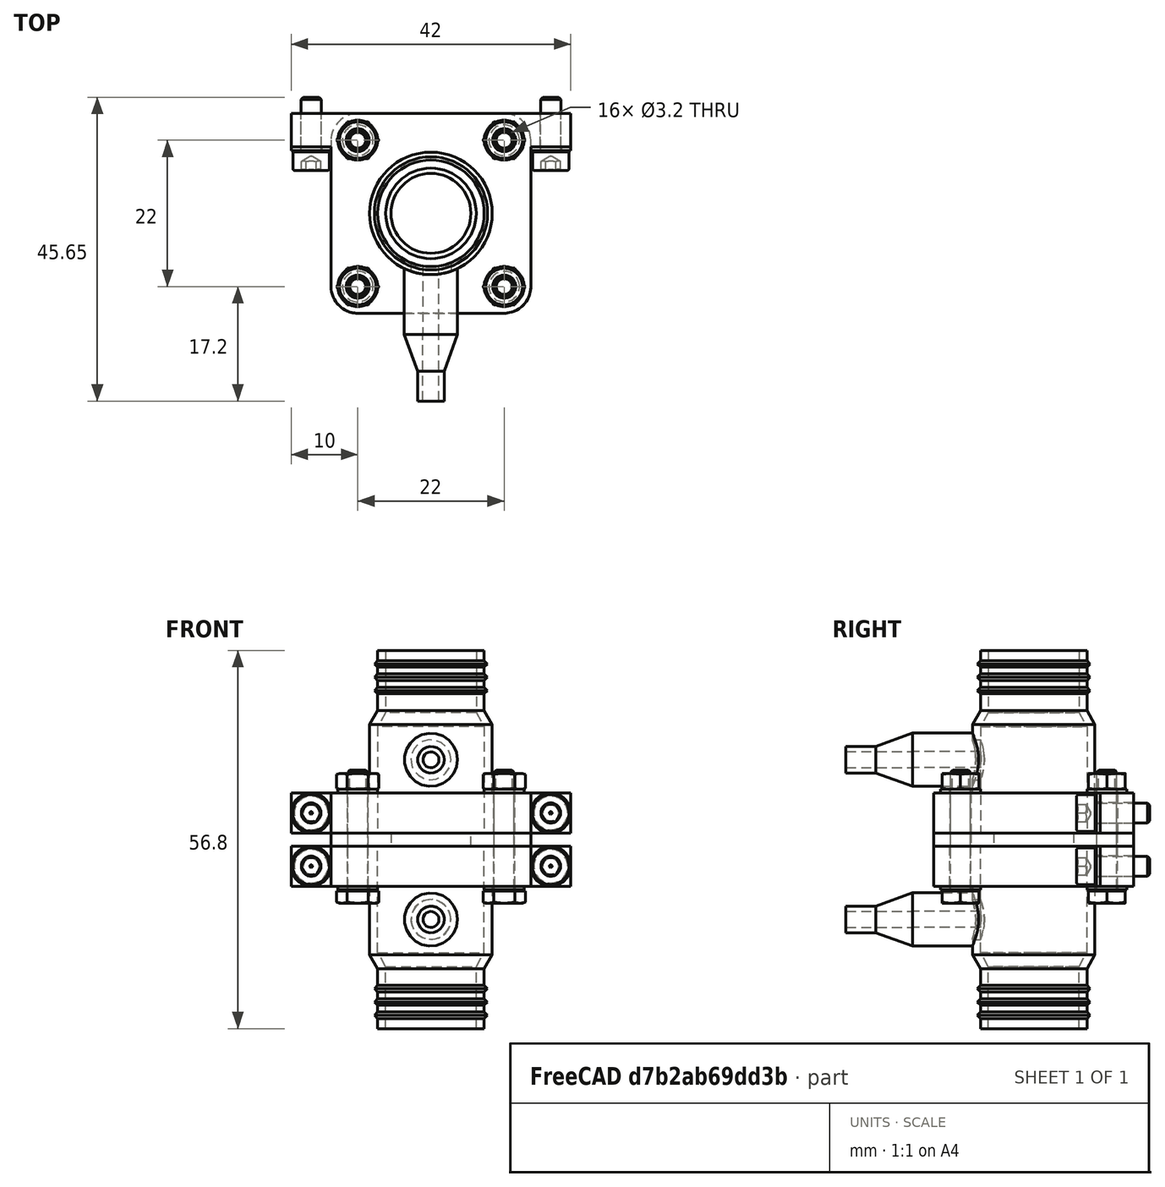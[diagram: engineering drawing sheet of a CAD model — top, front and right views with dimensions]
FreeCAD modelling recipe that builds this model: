
FCSTD DOCUMENT  (FreeCAD 0.19R20655 (Git))
Label: flowmeter_assembly
License: All rights reserved
LicenseURL: http://en.wikipedia.org/wiki/All_rights_reserved
objects: Part::FeaturePython×29, App::FeaturePython×18
note: 29 computed .brp shape members not serialized (recipe doc carries the construction recipe); baked Part::Feature solids carry a one-line shape summary decoded from their .brp

FEATURE [Part::FeaturePython] b_housing_001_  label="housing_001"  # a2plus imported part (geometry in sourceFile) (typed FeaturePython)
  a2p_Version = V0.1
  fixedPosition = true
  objectType = a2pPart
  sourceFile = .\housing.FCStd
  subassemblyImport = false
  timeLastImport = 1.58808e+09
  updateColors = true
FEATURE [Part::FeaturePython] b_gasket_001_  label="orifice_001"  # a2plus imported part (geometry in sourceFile) (typed FeaturePython)
  Placement = pos=(-3.70546e-08,-3.70546e-08,-2) rot=(0,0,1;0rad)
  a2p_Version = V0.1
  fixedPosition = false
  objectType = a2pPart
  sourceFile = .\gasket.FCStd
  subassemblyImport = false
  timeLastImport = 1.58802e+09
  updateColors = true
FEATURE [App::FeaturePython] axisCoincident_001  label="axisCoincident_001__housing_001"  # a2plus constraint (typed FeaturePython)
  Object1 = b_gasket_001_
  Object2 = b_housing_001_
  ParentTreeObject = -> b_gasket_001_
  SubElement1 = Face11
  SubElement2 = Face13
  Suppressed = false
  Type = axial
  directionConstraint = 0
  lockRotation = false
  suppressed = false
FEATURE [App::FeaturePython] axisCoincident_001_mirror  label="axisCoincident_001__gasket_001"  # a2plus constraint (typed FeaturePython)
  Object1 = b_gasket_001_
  Object2 = b_housing_001_
  ParentTreeObject = -> b_housing_001_
  SubElement1 = Face11
  SubElement2 = Face13
  Suppressed = false
  Type = axial
  directionConstraint = 0
  lockRotation = false
  suppressed = false
FEATURE [App::FeaturePython] axisCoincident_002  label="axisCoincident_002__housing_001"  # a2plus constraint (typed FeaturePython)
  Object1 = b_gasket_001_
  Object2 = b_housing_001_
  ParentTreeObject = -> b_gasket_001_
  SubElement1 = Face13
  SubElement2 = Face17
  Suppressed = false
  Type = axial
  directionConstraint = 0
  lockRotation = false
  suppressed = false
FEATURE [App::FeaturePython] axisCoincident_002_mirror  label="axisCoincident_002__gasket_001"  # a2plus constraint (typed FeaturePython)
  Object1 = b_gasket_001_
  Object2 = b_housing_001_
  ParentTreeObject = -> b_housing_001_
  SubElement1 = Face13
  SubElement2 = Face17
  Suppressed = false
  Type = axial
  directionConstraint = 0
  lockRotation = false
  suppressed = false
FEATURE [App::FeaturePython] planeCoincident_001  label="planeCoincident_001__housing_001"  # a2plus constraint (typed FeaturePython)
  Object1 = b_gasket_001_
  Object2 = b_housing_001_
  ParentTreeObject = -> b_gasket_001_
  SubElement1 = Face5
  SubElement2 = Face2
  Suppressed = false
  Type = plane
  directionConstraint = 1
  offset = 0
  suppressed = false
FEATURE [App::FeaturePython] planeCoincident_001_mirror  label="planeCoincident_001__gasket_001"  # a2plus constraint (typed FeaturePython)
  Object1 = b_gasket_001_
  Object2 = b_housing_001_
  ParentTreeObject = -> b_housing_001_
  SubElement1 = Face5
  SubElement2 = Face2
  Suppressed = false
  Type = plane
  directionConstraint = 1
  offset = 0
  suppressed = false
FEATURE [Part::FeaturePython] b_housing_001_001  label="housing_002"  # a2plus imported part (geometry in sourceFile) (typed FeaturePython)
  Placement = pos=(1.75624e-07,1e-15,-2) rot=(0,1,0;3.14159rad)
  a2p_Version = V0.1
  fixedPosition = false
  objectType = a2pPart
  sourceFile = .\housing.FCStd
  subassemblyImport = false
  timeLastImport = 1.58808e+09
  updateColors = true
FEATURE [App::FeaturePython] axisCoincident_003  label="axisCoincident_003__housing_001"  # a2plus constraint (typed FeaturePython)
  Object1 = b_housing_001_001
  Object2 = b_housing_001_
  ParentTreeObject = -> b_housing_001_001
  SubElement1 = Face18
  SubElement2 = Face13
  Suppressed = false
  Type = axial
  directionConstraint = 0
  lockRotation = false
  suppressed = false
FEATURE [App::FeaturePython] axisCoincident_003_mirror  label="axisCoincident_003__housing_002"  # a2plus constraint (typed FeaturePython)
  Object1 = b_housing_001_001
  Object2 = b_housing_001_
  ParentTreeObject = -> b_housing_001_
  SubElement1 = Face18
  SubElement2 = Face13
  Suppressed = false
  Type = axial
  directionConstraint = 0
  lockRotation = false
  suppressed = false
FEATURE [App::FeaturePython] planeCoincident_002  label="planeCoincident_002__gasket_001"  # a2plus constraint (typed FeaturePython)
  Object1 = b_housing_001_001
  Object2 = b_gasket_001_
  ParentTreeObject = -> b_housing_001_001
  SubElement1 = Face2
  SubElement2 = Face2
  Suppressed = false
  Type = plane
  directionConstraint = 0
  offset = 0
  suppressed = false
FEATURE [App::FeaturePython] planeCoincident_002_mirror  label="planeCoincident_002__housing_002"  # a2plus constraint (typed FeaturePython)
  Object1 = b_housing_001_001
  Object2 = b_gasket_001_
  ParentTreeObject = -> b_gasket_001_
  SubElement1 = Face2
  SubElement2 = Face2
  Suppressed = false
  Type = plane
  directionConstraint = 0
  offset = 0
  suppressed = false
FEATURE [App::FeaturePython] planeCoincident_003  label="planeCoincident_003__housing_002"  # a2plus constraint (typed FeaturePython)
  Object1 = b_housing_001_
  Object2 = b_housing_001_001
  ParentTreeObject = -> b_housing_001_
  SubElement1 = Face1
  SubElement2 = Face1
  Suppressed = false
  Type = plane
  directionConstraint = 0
  offset = 0
  suppressed = false
FEATURE [App::FeaturePython] planeCoincident_003_mirror  label="planeCoincident_003__housing_001"  # a2plus constraint (typed FeaturePython)
  Object1 = b_housing_001_
  Object2 = b_housing_001_001
  ParentTreeObject = -> b_housing_001_001
  SubElement1 = Face1
  SubElement2 = Face1
  Suppressed = false
  Type = plane
  directionConstraint = 0
  offset = 0
  suppressed = false
FEATURE [Part::FeaturePython] b_pressure_connector_001_  label="pressure_connector_001"  # a2plus imported part (geometry in sourceFile) (typed FeaturePython)
  Placement = pos=(2.53008e-09,-8.2,-13) rot=(1,0,0;1.5708rad)
  a2p_Version = V0.1
  fixedPosition = false
  objectType = a2pPart
  sourceFile = .\pressure_connector.FCStd
  subassemblyImport = false
  timeLastImport = 1.58808e+09
  updateColors = true
FEATURE [App::FeaturePython] axisCoincident_004  label="axisCoincident_004__housing_002"  # a2plus constraint (typed FeaturePython)
  Object1 = b_pressure_connector_001_
  Object2 = b_housing_001_001
  ParentTreeObject = -> b_pressure_connector_001_
  SubElement1 = Face3
  SubElement2 = Face22
  Suppressed = false
  Type = axial
  directionConstraint = 0
  lockRotation = false
  suppressed = false
FEATURE [App::FeaturePython] axisCoincident_004_mirror  label="axisCoincident_004__pressure_connector_001"  # a2plus constraint (typed FeaturePython)
  Object1 = b_pressure_connector_001_
  Object2 = b_housing_001_001
  ParentTreeObject = -> b_housing_001_001
  SubElement1 = Face3
  SubElement2 = Face22
  Suppressed = false
  Type = axial
  directionConstraint = 0
  lockRotation = false
  suppressed = false
FEATURE [App::FeaturePython] axisCoincident_005  label="axisCoincident_005__pressure_connector_001"  # a2plus constraint (typed FeaturePython)
  Object1 = b_housing_001_001
  Object2 = b_pressure_connector_001_
  ParentTreeObject = -> b_housing_001_001
  SubElement1 = Face18
  SubElement2 = Face5
  Suppressed = false
  Type = axial
  directionConstraint = 1
  lockRotation = false
  suppressed = false
FEATURE [App::FeaturePython] axisCoincident_005_mirror  label="axisCoincident_005__housing_002"  # a2plus constraint (typed FeaturePython)
  Object1 = b_housing_001_001
  Object2 = b_pressure_connector_001_
  ParentTreeObject = -> b_pressure_connector_001_
  SubElement1 = Face18
  SubElement2 = Face5
  Suppressed = false
  Type = axial
  directionConstraint = 1
  lockRotation = false
  suppressed = false
FEATURE [Part::FeaturePython] b_pressure_connector_001_001  label="pressure_connector_002"  # a2plus imported part (geometry in sourceFile) (typed FeaturePython)
  Placement = pos=(-9e-15,-8.20001,11) rot=(1,0,0;1.5708rad)
  a2p_Version = V0.1
  fixedPosition = false
  objectType = a2pPart
  sourceFile = .\pressure_connector.FCStd
  subassemblyImport = false
  timeLastImport = 1.58808e+09
  updateColors = true
FEATURE [App::FeaturePython] axisCoincident_006  label="axisCoincident_006__housing_001"  # a2plus constraint (typed FeaturePython)
  Object1 = b_pressure_connector_001_001
  Object2 = b_housing_001_
  ParentTreeObject = -> b_pressure_connector_001_001
  SubElement1 = Face3
  SubElement2 = Face22
  Suppressed = false
  Type = axial
  directionConstraint = 0
  lockRotation = false
  suppressed = false
FEATURE [App::FeaturePython] axisCoincident_006_mirror  label="axisCoincident_006__pressure_connector_002"  # a2plus constraint (typed FeaturePython)
  Object1 = b_pressure_connector_001_001
  Object2 = b_housing_001_
  ParentTreeObject = -> b_housing_001_
  SubElement1 = Face3
  SubElement2 = Face22
  Suppressed = false
  Type = axial
  directionConstraint = 0
  lockRotation = false
  suppressed = false
FEATURE [Part::FeaturePython] Washer  label="M3-Washer"  # Fasteners workbench fastener (typed FeaturePython)
  Placement = pos=(18,10,-5) rot=(1,0,0;1.5708rad)
  baseObject = -> b_housing_001_001 [Edge37]
  diameter = 4
  invert = false
  matchOuter = true
  offset = 0
  type = 2
FEATURE [Part::FeaturePython] Washer001  label="M3-Washer001"  # Fasteners workbench fastener (typed FeaturePython)
  Placement = pos=(-18,10,-5) rot=(1,0,0;1.5708rad)
  baseObject = -> b_housing_001_001 [Edge44]
  diameter = 4
  invert = false
  matchOuter = true
  offset = 0
  type = 2
FEATURE [Part::FeaturePython] Washer002  label="M3-Washer002"  # Fasteners workbench fastener (typed FeaturePython)
  Placement = pos=(18,10,3) rot=(1,0,0;1.5708rad)
  baseObject = -> b_housing_001_ [Edge44]
  diameter = 4
  invert = false
  matchOuter = true
  offset = 0
  type = 2
FEATURE [Part::FeaturePython] Washer003  label="M3-Washer003"  # Fasteners workbench fastener (typed FeaturePython)
  Placement = pos=(-18,10,3) rot=(1,0,0;1.5708rad)
  baseObject = -> b_housing_001_ [Edge37]
  diameter = 4
  invert = false
  matchOuter = true
  offset = 0
  type = 2
FEATURE [Part::FeaturePython] Washer004  label="M3-Washer004"  # Fasteners workbench fastener (typed FeaturePython)
  Placement = pos=(11,11,-8) rot=(0,-1,0;3.14159rad)
  baseObject = -> b_housing_001_001 [Edge31]
  diameter = 4
  invert = false
  matchOuter = true
  offset = 0
  type = 2
FEATURE [Part::FeaturePython] Washer005  label="M3-Washer005"  # Fasteners workbench fastener (typed FeaturePython)
  Placement = pos=(11,-11,-8) rot=(0,-1,0;3.14159rad)
  baseObject = -> b_housing_001_001 [Edge34]
  diameter = 4
  invert = false
  matchOuter = true
  offset = 0
  type = 2
FEATURE [Part::FeaturePython] Washer006  label="M3-Washer006"  # Fasteners workbench fastener (typed FeaturePython)
  Placement = pos=(-11,-11,-8) rot=(0,-1,0;3.14159rad)
  baseObject = -> b_housing_001_001 [Edge33]
  diameter = 4
  invert = false
  matchOuter = true
  offset = 0
  type = 2
FEATURE [Part::FeaturePython] Washer007  label="M3-Washer007"  # Fasteners workbench fastener (typed FeaturePython)
  Placement = pos=(-11,11,-8) rot=(0,-1,0;3.14159rad)
  baseObject = -> b_housing_001_001 [Edge32]
  diameter = 4
  invert = false
  matchOuter = true
  offset = 0
  type = 2
FEATURE [Part::FeaturePython] Washer008  label="M3-Washer008"  # Fasteners workbench fastener (typed FeaturePython)
  Placement = pos=(-11,-11,6) rot=(0,0,1;0rad)
  baseObject = -> b_housing_001_ [Edge34]
  diameter = 4
  invert = false
  matchOuter = true
  offset = 0
  type = 2
FEATURE [Part::FeaturePython] Washer009  label="M3-Washer009"  # Fasteners workbench fastener (typed FeaturePython)
  Placement = pos=(-11,11,6) rot=(0,0,1;0rad)
  baseObject = -> b_housing_001_ [Edge31]
  diameter = 4
  invert = false
  matchOuter = true
  offset = 0
  type = 2
FEATURE [Part::FeaturePython] Washer010  label="M3-Washer010"  # Fasteners workbench fastener (typed FeaturePython)
  Placement = pos=(11,-11,6) rot=(0,0,1;0rad)
  baseObject = -> b_housing_001_ [Edge33]
  diameter = 4
  invert = false
  matchOuter = true
  offset = 0
  type = 2
FEATURE [Part::FeaturePython] Washer011  label="M3-Washer011"  # Fasteners workbench fastener (typed FeaturePython)
  Placement = pos=(11,11,6) rot=(0,0,1;0rad)
  baseObject = -> b_housing_001_ [Edge32]
  diameter = 4
  invert = false
  matchOuter = true
  offset = 0
  type = 2
FEATURE [Part::FeaturePython] Nut  label="M3-Nut"  # Fasteners workbench fastener (typed FeaturePython)
  Placement = pos=(-11,-11,6.55) rot=(0,0,1;0rad)
  baseObject = -> Washer008 [Edge1]
  diameter = 4
  invert = false
  matchOuter = true
  offset = 0
  thread = false
  type = 4
FEATURE [Part::FeaturePython] Nut001  label="M3-Nut001"  # Fasteners workbench fastener (typed FeaturePython)
  Placement = pos=(11,-11,6.55) rot=(0,0,1;0rad)
  baseObject = -> Washer010 [Edge1]
  diameter = 4
  invert = false
  matchOuter = true
  offset = 0
  thread = false
  type = 4
FEATURE [Part::FeaturePython] Nut002  label="M3-Nut002"  # Fasteners workbench fastener (typed FeaturePython)
  Placement = pos=(-11,11,6.55) rot=(0,0,1;0rad)
  baseObject = -> Washer009 [Edge1]
  diameter = 4
  invert = false
  matchOuter = true
  offset = 0
  thread = false
  type = 4
FEATURE [Part::FeaturePython] Nut003  label="M3-Nut003"  # Fasteners workbench fastener (typed FeaturePython)
  Placement = pos=(11,11,6.55) rot=(0,0,1;0rad)
  baseObject = -> Washer011 [Edge1]
  diameter = 4
  invert = false
  matchOuter = true
  offset = 0
  thread = false
  type = 4
FEATURE [Part::FeaturePython] Screw004  label="M3x18-Screw"  # Fasteners workbench fastener (typed FeaturePython)
  Placement = pos=(-11,-11,-8.55) rot=(-1,0,0;3.14159rad)
  baseObject = -> Washer006 [Edge1]
  diameter = 4
  invert = false
  length = 3
  lengthCustom = 18
  matchOuter = true
  offset = 0
  thread = false
  type = 14
FEATURE [Part::FeaturePython] Screw005  label="M3x18-Screw002"  # Fasteners workbench fastener (typed FeaturePython)
  Placement = pos=(-11,11,-8.55) rot=(-1,0,0;3.14159rad)
  baseObject = -> Washer007 [Edge1]
  diameter = 4
  invert = false
  length = 3
  lengthCustom = 18
  matchOuter = true
  offset = 0
  thread = false
  type = 14
FEATURE [Part::FeaturePython] Screw006  label="M3x18-Screw001"  # Fasteners workbench fastener (typed FeaturePython)
  Placement = pos=(11,-11,-8.55) rot=(-1,0,0;3.14159rad)
  baseObject = -> Washer005 [Edge1]
  diameter = 4
  invert = false
  length = 3
  lengthCustom = 18
  matchOuter = true
  offset = 0
  thread = false
  type = 14
FEATURE [Part::FeaturePython] Screw007  label="M3x18-Screw003"  # Fasteners workbench fastener (typed FeaturePython)
  Placement = pos=(11,11,-8.55) rot=(-1,0,0;3.14159rad)
  baseObject = -> Washer004 [Edge1]
  diameter = 4
  invert = false
  length = 3
  lengthCustom = 18
  matchOuter = true
  offset = 0
  thread = false
  type = 14
FEATURE [Part::FeaturePython] Screw  label="M3x8-Screw"  # Fasteners workbench fastener (typed FeaturePython)
  Placement = pos=(-18,9.45,3) rot=(1,0,0;1.5708rad)
  baseObject = -> Washer003 [Edge1]
  diameter = 4
  invert = false
  length = 2
  lengthCustom = 8
  matchOuter = true
  offset = 0
  thread = false
  type = 16
FEATURE [Part::FeaturePython] Screw008  label="M3x8-Screw001"  # Fasteners workbench fastener (typed FeaturePython)
  Placement = pos=(-18,9.45,-5) rot=(1,0,0;1.5708rad)
  baseObject = -> Washer001 [Edge1]
  diameter = 4
  invert = false
  length = 2
  lengthCustom = 8
  matchOuter = true
  offset = 0
  thread = false
  type = 16
FEATURE [Part::FeaturePython] Screw009  label="M3x8-Screw003"  # Fasteners workbench fastener (typed FeaturePython)
  Placement = pos=(18,9.45,-5) rot=(1,0,0;1.5708rad)
  baseObject = -> Washer [Edge1]
  diameter = 4
  invert = false
  length = 2
  lengthCustom = 8
  matchOuter = true
  offset = 0
  thread = false
  type = 16
FEATURE [Part::FeaturePython] Screw010  label="M3x8-Screw002"  # Fasteners workbench fastener (typed FeaturePython)
  Placement = pos=(18,9.45,3) rot=(1,0,0;1.5708rad)
  baseObject = -> Washer002 [Edge1]
  diameter = 4
  invert = false
  length = 2
  lengthCustom = 8
  matchOuter = true
  offset = 0
  thread = false
  type = 16
